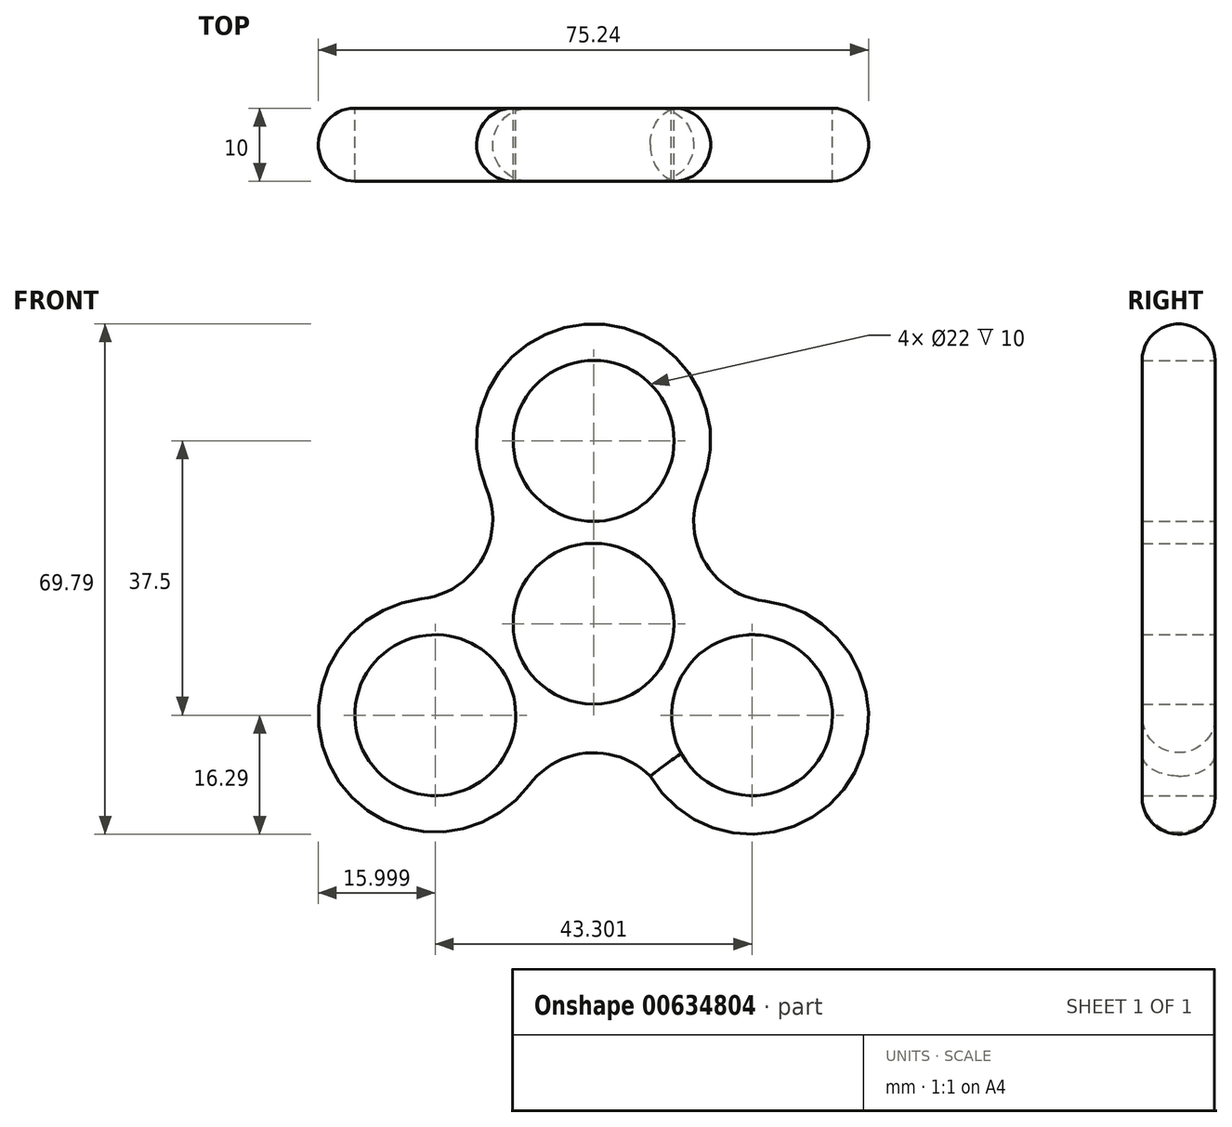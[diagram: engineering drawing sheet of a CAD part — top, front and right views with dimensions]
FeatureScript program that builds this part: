
annotation { "Feature Type Name" : "Feature", "Feature Type Description" : "" }
export const myFeature = defineFeature(function(context is Context, id is Id, definition is map)
    precondition{}
    {
        {
            var Q0;
            Q0=qCreatedBy(makeId("Front.planeOp"),FACE);
            var sketch = newSketch(context, id + "F0", { "sketchPlane" : qUnion([Q0])});
            skCircle(sketch, "E0.cCircle", {"center": v(0, 0) * mm, "radius": 25 * mm, "construction": true});
            skCircle(sketch, "E1", {"center": v(0, 0) * mm, "radius": 11 * mm});
            skCircle(sketch, "E2", {"center": v(0, 25) * mm, "radius": 11 * mm});
            skCircle(sketch, "E3", {"center": v(-21.65, -12.5) * mm, "radius": 11 * mm});
            skCircle(sketch, "E4", {"center": v(21.65, -12.5) * mm, "radius": 11 * mm});
            skArc(sketch, "E5", {"start": v(14.62, 18.5) * mm, "mid": v(0.1, 41) * mm, "end": v(-14.7, 18.67) * mm});
            skArc(sketch, "E6", {"start": v(-10.99, -0.57) * mm, "mid": v(-12.27, 0.46) * mm, "end": v(-13.65, 1.36) * mm});
            skArc(sketch, "E7", {"start": v(-24.78, 3.32) * mm, "mid": v(-15.27, 8.82) * mm, "end": v(-15.26, 19.8) * mm});
            skArc(sketch, "E8", {"start": v(15.3, 19.78) * mm, "mid": v(14.78, 9.21) * mm, "end": v(23.41, 3.1) * mm});
            skArc(sketch, "E9", {"start": v(9.52, -23.12) * mm, "mid": v(0, -17.63) * mm, "end": v(-9.52, -23.12) * mm});
            skArc(sketch, "E10.trimOffspring", {"start": v(-23.51, 3.4) * mm, "mid": v(-35.5, -20.5) * mm, "end": v(-8.82, -22.06) * mm});
            skArc(sketch, "E11.trimOffspring", {"start": v(5.99, -9.23) * mm, "mid": v(30.83, -25.86) * mm, "end": v(23.41, 3.1) * mm});
            skSolve(sketch);
        }
        {
            var Q0;
            Q0=makeQuery(id+"F0.imprint","IMPRINT",FACE,{"disambiguationData":[TD([[makeQuery(id+"F0.imprint","IMPRINT",EDGE,{"derivedFrom":sQuery(id+"F0.wireOp",EDGE,"E2")}),-1.0]])]});
            extrude(context, id + "F1", {"entities" : qUnion([Q0]), "depth" : 5 * mm, "offsetDistance" : 25 * mm, "hasSecondDirection" : true, "secondDirectionOppositeDirection" : true, "secondDirectionDepth" : 5 * mm});
        }
        {
            var Q0;
            Q0=makeQuery(id+"F1.opExtrude","CAP_EDGE",EDGE,{"disambiguationData":[OSD([sQuery(id+"F0.wireOp",EDGE,"E5")])],"isStart":true});
            var Q1;
            Q1=makeQuery(id+"F1.opExtrude","CAP_EDGE",EDGE,{"disambiguationData":[OSD([sQuery(id+"F0.wireOp",EDGE,"E8")])],"isStart":true});
            var Q2;
            Q2=makeQuery(id+"F1.opExtrude","CAP_EDGE",EDGE,{"disambiguationData":[OSD([sQuery(id+"F0.wireOp",EDGE,"E11.trimOffspring")])],"isStart":false});
            fillet(context, id + "F2", {"entities" : qUnion([Q0, Q1, Q2]), "radius" : 5 * mm, "tangentPropagation" : true, "allowEdgeOverflow" : false});
        }
    });
